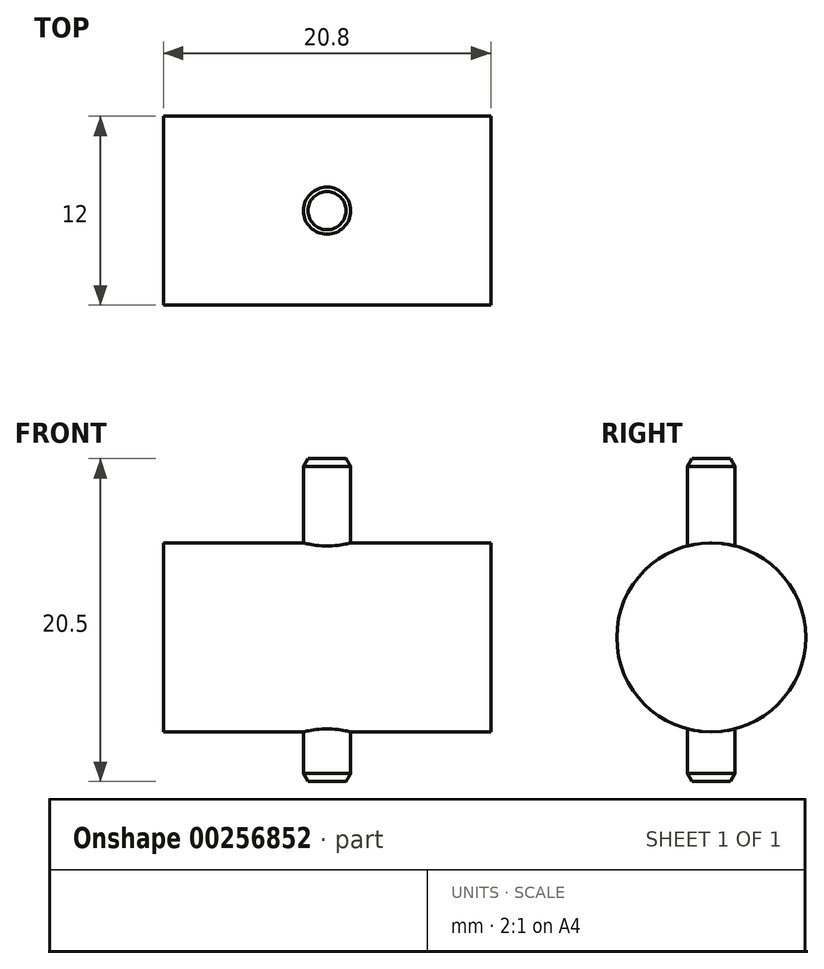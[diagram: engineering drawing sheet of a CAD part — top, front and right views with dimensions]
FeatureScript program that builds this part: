
annotation { "Feature Type Name" : "Feature", "Feature Type Description" : "" }
export const myFeature = defineFeature(function(context is Context, id is Id, definition is map)
    precondition{}
    {
        {
            var Q0;
            Q0=qCreatedBy(makeId("Right.planeOp"),FACE);
            var sketch = newSketch(context, id + "F0", { "sketchPlane" : qUnion([Q0])});
            skCircle(sketch, "E0", {"center": v(0, 0) * mm, "radius": 6 * mm});
            skSolve(sketch);
        }
        {
            var Q0;
            Q0 = qSketchRegion(id + "F0", true);
            extrude(context, id + "F1", {"entities" : qUnion([Q0]), "endBound" : BoundingType.SYMMETRIC, "depth" : 20.8 * mm});
        }
        {
            var Q0;
            Q0=qCreatedBy(makeId("Top.planeOp"),FACE);
            var sketch = newSketch(context, id + "F2", { "sketchPlane" : qUnion([Q0])});
            skCircle(sketch, "E1", {"center": v(0, 0) * mm, "radius": 1.5 * mm});
            skSolve(sketch);
        }
        {
            var Q0;
            Q0 = qSketchRegion(id + "F2", true);
            extrude(context, id + "F3", {"entities" : qUnion([Q0]), "operationType" : NewBodyOperationType.REMOVE, "endBound" : BoundingType.SYMMETRIC, "oppositeDirection" : true, "depth" : 25.4 * mm});
        }
        {
            var Q0;
            Q0=qCreatedBy(makeId("Right.planeOp"),FACE);
            var sketch = newSketch(context, id + "F4", { "sketchPlane" : qUnion([Q0])});
            skLineSegment(sketch, "E2", {"start": v(0, 14.92) * mm, "end": v(0, -10.62) * mm, "construction": true});
            skLineSegment(sketch, "E3", {"start": v(0, -9.14) * mm, "end": v(1.21, -9.14) * mm});
            skLineSegment(sketch, "E4", {"start": v(1.21, -9.14) * mm, "end": v(1.5, -8.64) * mm});
            skLineSegment(sketch, "E5", {"start": v(1.5, -8.64) * mm, "end": v(1.5, 10.86) * mm});
            skLineSegment(sketch, "E6", {"start": v(1.5, 10.86) * mm, "end": v(1.21, 11.36) * mm});
            skLineSegment(sketch, "E7", {"start": v(1.21, 11.36) * mm, "end": v(0, 11.36) * mm});
            skLineSegment(sketch, "E8", {"start": v(0, 11.36) * mm, "end": v(0, -9.14) * mm});
            skSolve(sketch);
        }
        {
            var Q0;
            Q0 = qSketchRegion(id + "F4", true);
            var Q1;
            Q1=sQuery(id+"F4.wireOp",EDGE,"E2");
            revolve(context, id + "F5", {"operationType" : NewBodyOperationType.ADD, "entities" : qUnion([Q0]), "axis" : qUnion([Q1]), "revolveType" : RevolveType.FULL});
        }
    });
